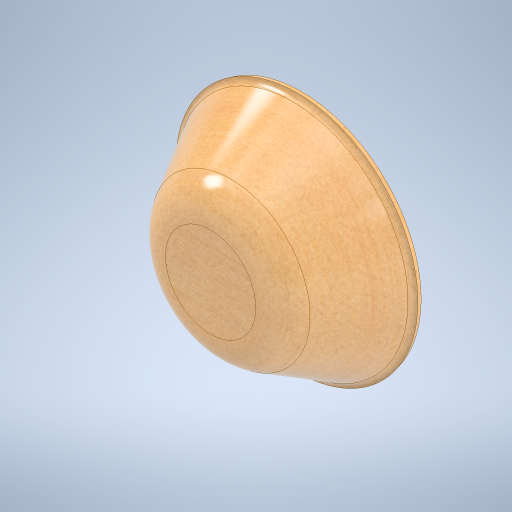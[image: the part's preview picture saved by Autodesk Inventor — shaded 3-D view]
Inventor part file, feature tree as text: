
AUTODESK INVENTOR PART (.ipt)
format: ipt  version: 2024 (Build 280153000, 153)  size: 410,624 bytes
history: native  units: mm
features: revolve x1, fillet x1, shell x1, sketch x1
ambient origin geometry x8: Origin, YZ Plane, XZ Plane, XY Plane, X Axis, Y Axis, Z Axis, Center Point
bodies: Volumenkörper1 (feature_tree)
feature tree (4):
  revolve  "Umdrehung1"
  fillet  "Rundung2"  [1 undecoded]
  shell  "Wandung5"  Thickness=80.0mm
  sketch  "Skizze1"  dims[d3=120.0mm d4=2.0mm d5=8.0mm d6=90.0deg d12=35.0mm d13=4.0mm d14=0.0mm d15=0.0mm]
note: 1 required parameter value undecoded (feature->parameter linkage not recoverable at this tier; creation-order binding heuristic only, values carry confidence <= 0.55)
